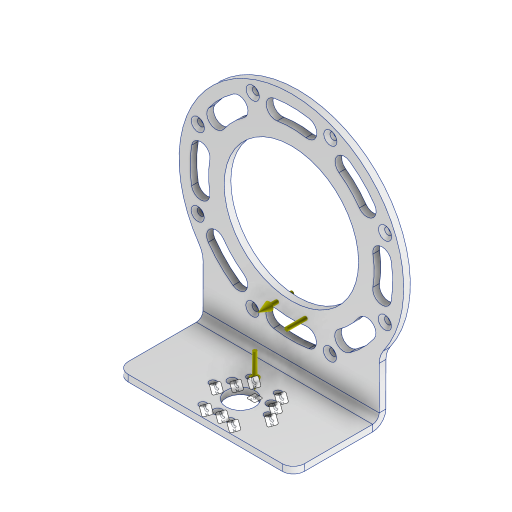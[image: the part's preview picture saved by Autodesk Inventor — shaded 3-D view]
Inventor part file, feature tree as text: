
AUTODESK INVENTOR PART (.ipt)
format: ipt  version: 2023 (Build 270158000, 158)  size: 1,620,992 bytes
history: native  units: mm
features: other x10, sketch x6, extrude x3, fillet x3, hole x1
ambient origin geometry x8: Origin, YZ Plane, XZ Plane, XY Plane, X Axis, Y Axis, Z Axis, Center Point
bodies: Body1 (feature_tree), Body2 (feature_tree)
feature tree (23):
  other  "GIM8108-8_1.ipt"
  other  "ソリッド1"
  other  "フランジ1"
  extrude  "押し出し1"  Depth=10.0mm
  fillet  "フィレット1"  Radius=102.0mm
  fillet  "フィレット2"  Radius=80.0mm
  extrude  "押し出し6"  Depth=40.0mm
  extrude  "押し出し7"  Depth=18.0mm
  fillet  "フィレット3"  Radius=61.0mm
  hole  "穴1"  [1 undecoded]
  other  "TaggingFeature1"
  sketch  "スケッチ1"
  other  "プレート1"
  sketch  "スケッチ2"
  other  "プレート2"
  other  "曲げ1"
  other  "コーナー1"
  sketch  "スケッチ3"
  sketch  "スケッチ7"
  sketch  "スケッチ8"
  sketch  "スケッチ10"
  other  "ソリッド1::GIM8108-8_1.ipt"
  other  "Srf1"
note: 1 required parameter value undecoded (feature->parameter linkage not recoverable at this tier; creation-order binding heuristic only, values carry confidence <= 0.55)
